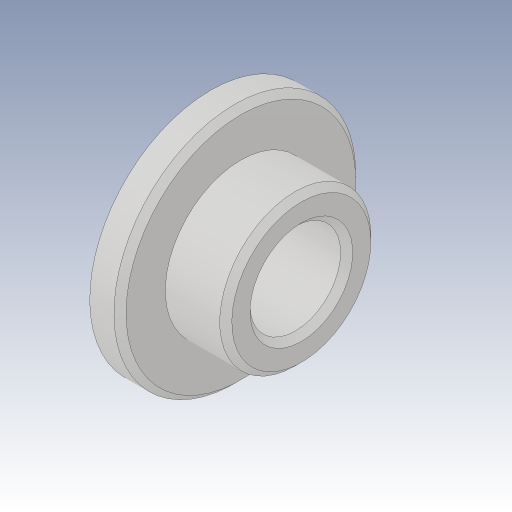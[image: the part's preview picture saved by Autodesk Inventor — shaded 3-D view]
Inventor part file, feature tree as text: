
AUTODESK INVENTOR PART (.ipt)
format: ipt  version: 2023.3 (Build 273359000, 359)  size: 162,304 bytes
history: native  units: in
note: dims shown in document units (in); Inventor stores cm internally (conversion verified against a paired STEP export)
features: revolve x1, chamfer x1, sketch x1
ambient origin geometry x8: Origin, YZ Plane, XZ Plane, XY Plane, X Axis, Y Axis, Z Axis, Center Point
bodies: Body1 (feature_tree)
feature tree (3):
  revolve  "Umdrehung1"
  chamfer  "Fase1"  Distance=0.1181in
  sketch  "Skizze3"  dims[d4=0.0394in d5=0.1181in d6=0.1181in d7=0.315in d8=0.1969in d9=90.0deg d10=0.0079in d11=0.0787in d12=45.0deg]
